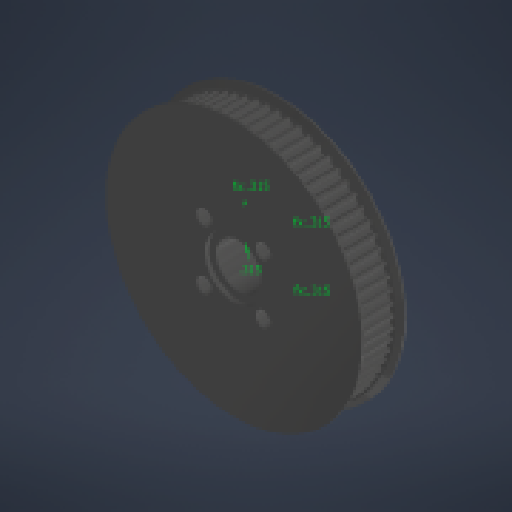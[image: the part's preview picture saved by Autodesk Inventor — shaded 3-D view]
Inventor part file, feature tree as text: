
AUTODESK INVENTOR PART (.ipt)
format: ipt  version: 2024.2 (Build 282272000, 272)  size: 1,467,904 bytes
history: native  units: in
note: dims shown in document units (in); Inventor stores cm internally (conversion verified against a paired STEP export)
features: other x2, extrude x1, sketch x1
ambient origin geometry x8: Origin, YZ Plane, XZ Plane, XY Plane, X Axis, Y Axis, Z Axis, Center Point
bodies: Body1 (feature_tree)
feature tree (4):
  other  "Thin_70T.step"
  extrude  "Extrusion4"  Depth=0.315in
  sketch  "Sketch5"  dims[d13=0.315in d14=0.315in d15=0.315in d16=0.315in d17=0.0984in d18=0.0in]
  other  "[LS] Pulley HTD3 70T"
